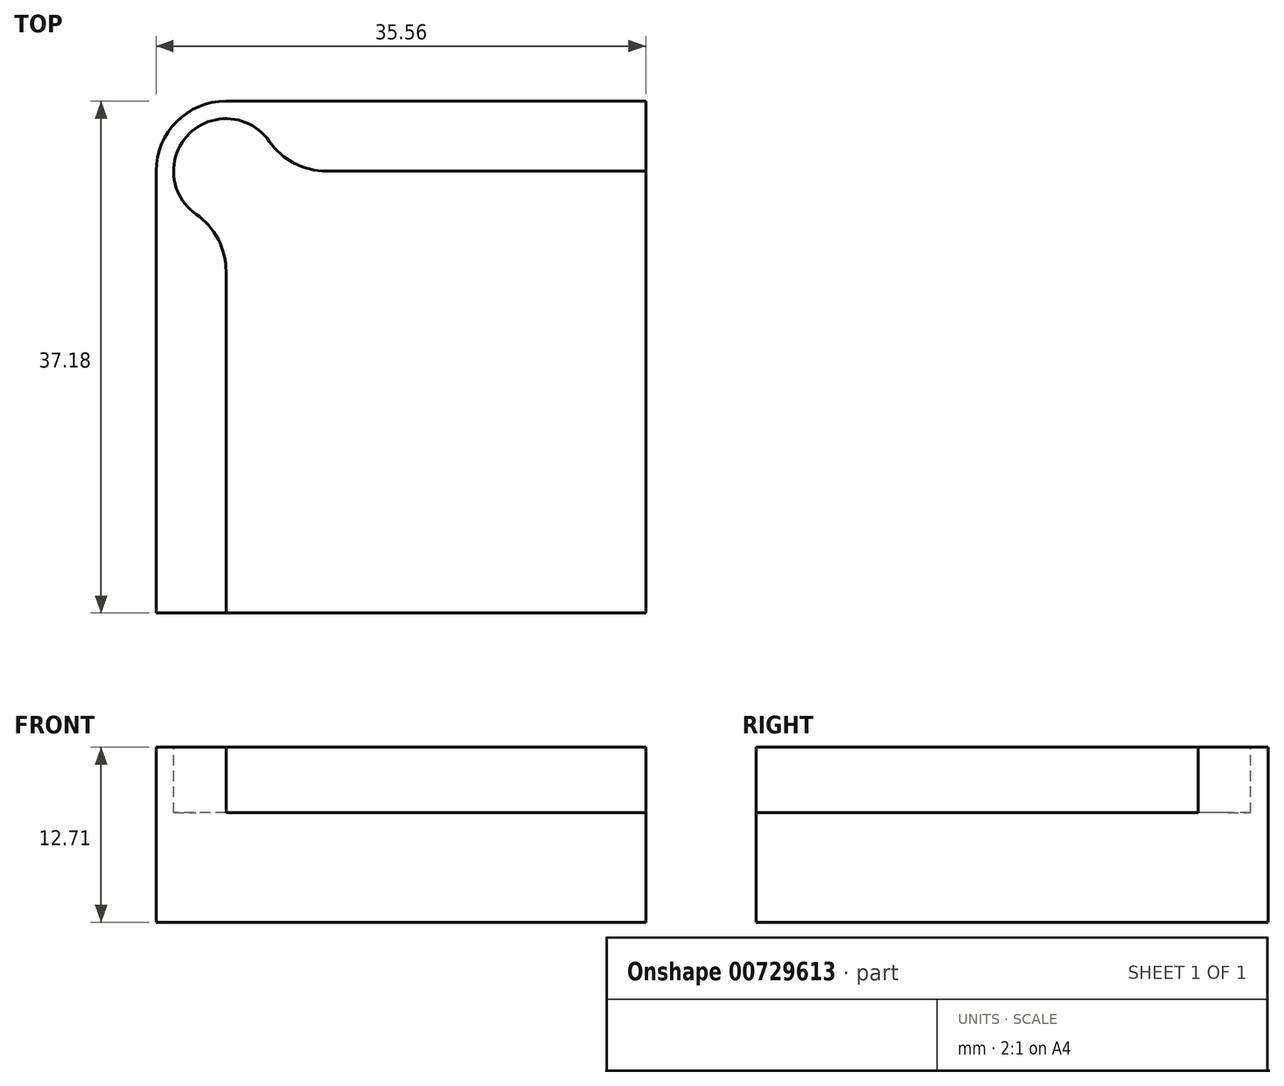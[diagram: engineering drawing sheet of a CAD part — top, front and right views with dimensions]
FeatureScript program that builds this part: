
annotation { "Feature Type Name" : "Feature", "Feature Type Description" : "" }
export const myFeature = defineFeature(function(context is Context, id is Id, definition is map)
    precondition{}
    {
        {
            var Q0;
            Q0=qCreatedBy(makeId("Top.planeOp"),FACE);
            var sketch = newSketch(context, id + "F0", { "sketchPlane" : qUnion([Q0])});
            skLineSegment(sketch, "E0.bottom", {"start": v(17.78, 18.59) * mm, "end": v(-17.78, 18.59) * mm});
            skLineSegment(sketch, "E0.top", {"start": v(17.78, -18.59) * mm, "end": v(-17.78, -18.59) * mm});
            skLineSegment(sketch, "E0.left", {"start": v(17.78, 18.59) * mm, "end": v(17.78, -18.59) * mm});
            skLineSegment(sketch, "E0.right", {"start": v(-17.78, 18.59) * mm, "end": v(-17.78, -18.59) * mm});
            skPoint(sketch, "E0.middle", {"position": v(0, 0) * mm});
            skSolve(sketch);
        }
        {
            var Q0;
            Q0=makeQuery(id+"F0.imprint","IMPRINT",FACE,{"disambiguationData":[TD([[makeQuery(id+"F0.imprint","IMPRINT",EDGE,{"derivedFrom":sQuery(id+"F0.wireOp",EDGE,"E0.bottom")}),1.0]])]});
            extrude(context, id + "F1", {"entities" : qUnion([Q0]), "depth" : 12.7 * mm + 3 / 406.4 * mm, "offsetDistance" : 25.4 * mm});
        }
        {
            var Q0;
            Q0=makeQuery(id+"F1.opExtrude","CAP_FACE",FACE,{"disambiguationData":[OSD([sQuery(id+"F0.wireOp",EDGE,"E0.bottom"),sQuery(id+"F0.wireOp",EDGE,"E0.top"),sQuery(id+"F0.wireOp",EDGE,"E0.left"),sQuery(id+"F0.wireOp",EDGE,"E0.right")])],"isStart":false});
            var sketch = newSketch(context, id + "F2", { "sketchPlane" : qUnion([Q0])});
            skLineSegment(sketch, "E1.bottom", {"start": v(17.78, -18.59) * mm, "end": v(-12.7, -18.59) * mm});
            skLineSegment(sketch, "E1.top", {"start": v(17.78, 13.5) * mm, "end": v(-8.89, 13.5) * mm});
            skLineSegment(sketch, "E1.left", {"start": v(17.78, -18.59) * mm, "end": v(17.78, 13.5) * mm});
            skLineSegment(sketch, "E1.right", {"start": v(-12.7, -18.59) * mm, "end": v(-12.7, 9.7) * mm});
            skArc(sketch, "E2", {"start": v(-8.89, 13.5) * mm, "mid": v(-15.4, 16.2) * mm, "end": v(-12.7, 9.7) * mm});
            skSolve(sketch);
        }
        {
            var Q0;
            Q0=makeQuery(id+"F2.imprint","IMPRINT",FACE,{"disambiguationData":[TD([[makeQuery(id+"F2.imprint","IMPRINT",EDGE,{"derivedFrom":sQuery(id+"F2.wireOp",EDGE,"E1.bottom")}),-1.0]])]});
            extrude(context, id + "F3", {"entities" : qUnion([Q0]), "operationType" : NewBodyOperationType.REMOVE, "oppositeDirection" : true, "depth" : 4.76 * mm, "offsetDistance" : 25.4 * mm});
        }
        {
            var Q0;
            Q0=makeQuery(id+"F3.boolean.opBoolean","COPY",EDGE,{"derivedFrom":makeQuery(id+"F3.opExtrude","SWEPT_EDGE",EDGE,{"disambiguationData":[OSD([sQuery(id+"F2.wireOp",EDGE,"E1.right"),sQuery(id+"F2.wireOp",EDGE,"E2")])]})});
            var Q1;
            Q1=makeQuery(id+"F3.boolean.opBoolean","COPY",EDGE,{"derivedFrom":makeQuery(id+"F3.opExtrude","SWEPT_EDGE",EDGE,{"disambiguationData":[OSD([sQuery(id+"F2.wireOp",EDGE,"E1.top"),sQuery(id+"F2.wireOp",EDGE,"E2")])]})});
            fillet(context, id + "F4", {"entities" : qUnion([Q0, Q1]), "radius" : 5.08 * mm, "tangentPropagation" : true, "allowEdgeOverflow" : false});
        }
        {
            var Q0;
            Q0=makeQuery(id+"F1.opExtrude","SWEPT_EDGE",EDGE,{"disambiguationData":[OSD([sQuery(id+"F0.wireOp",EDGE,"E0.bottom"),sQuery(id+"F0.wireOp",EDGE,"E0.right")])]});
            fillet(context, id + "F5", {"entities" : qUnion([Q0]), "radius" : 5.08 * mm, "tangentPropagation" : true, "allowEdgeOverflow" : false});
        }
    });
